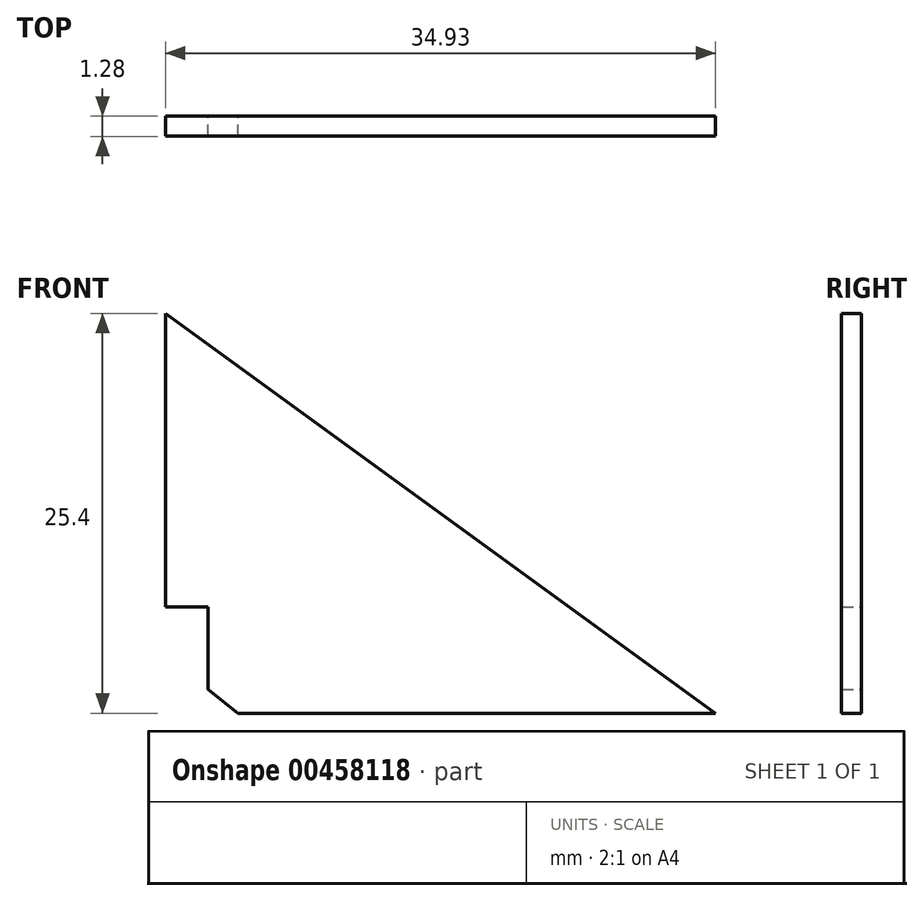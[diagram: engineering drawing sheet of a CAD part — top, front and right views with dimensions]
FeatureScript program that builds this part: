
annotation { "Feature Type Name" : "Feature", "Feature Type Description" : "" }
export const myFeature = defineFeature(function(context is Context, id is Id, definition is map)
    precondition{}
    {
        {
            var Q0;
            Q0=qCreatedBy(makeId("Front.planeOp"),FACE);
            var sketch = newSketch(context, id + "F0", { "sketchPlane" : qUnion([Q0])});
            skLineSegment(sketch, "E0", {"start": v(0, 6.77) * mm, "end": v(0, 25.4) * mm});
            skLineSegment(sketch, "E1", {"start": v(0, 25.4) * mm, "end": v(34.93, 0) * mm});
            skLineSegment(sketch, "E2", {"start": v(34.93, 0) * mm, "end": v(4.62, 0) * mm});
            skLineSegment(sketch, "E3", {"start": v(4.62, 0) * mm, "end": v(2.72, 1.5) * mm});
            skLineSegment(sketch, "E4", {"start": v(2.72, 1.5) * mm, "end": v(2.72, 6.77) * mm});
            skLineSegment(sketch, "E5", {"start": v(2.72, 6.77) * mm, "end": v(0, 6.77) * mm});
            skSolve(sketch);
        }
        {
            var Q0;
            Q0=makeQuery(id+"F0.imprint","IMPRINT",FACE,{"disambiguationData":[TD([[makeQuery(id+"F0.imprint","IMPRINT",EDGE,{"derivedFrom":sQuery(id+"F0.wireOp",EDGE,"E0")}),-1.0]])]});
            extrude(context, id + "F1", {"entities" : qUnion([Q0]), "endBound" : BoundingType.SYMMETRIC, "depth" : 1.27 * mm});
        }
    });
